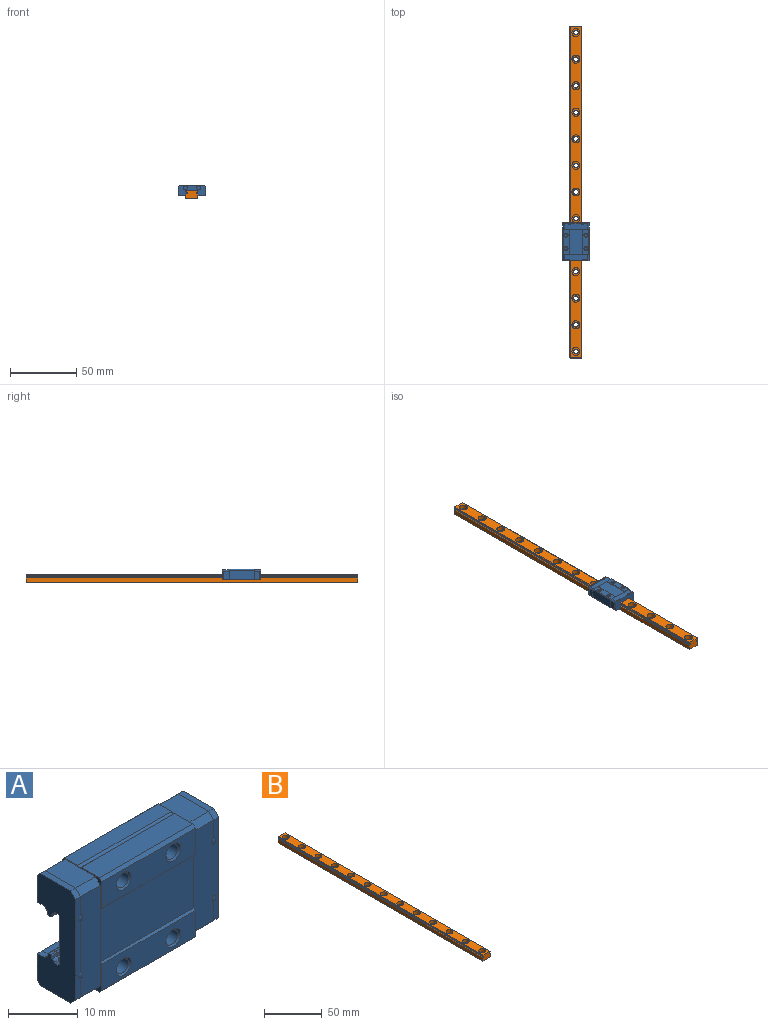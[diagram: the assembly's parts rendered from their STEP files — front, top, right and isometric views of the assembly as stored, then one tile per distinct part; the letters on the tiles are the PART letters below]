
ASSEMBLY  parts=2 mates=1
PART A: 239 faces, bbox 29x8.1x20.1 mm
  f0: plane 0.11x0.01mm, normal (0,0,1), area 0mm2, adj f1,f2,f238
  f1: revolved ~0.04x0.02mm, area 0mm2, adj f0,f2,f238
  f2: plane 17.72x5.12mm, normal (0,-1,0), area 86.8mm2, adj f0,f1,f3,f39,f40,f41,f42,f78
  f3: plane 4x1mm, normal (0,-0.71,0.71), area 5.7mm2, adj f2,f4,f87,f89
  f4: plane 6.1x4mm, normal (0,0,1), area 24.4mm2, adj f3,f5,f87,f89
  f5: plane 4x0.6mm, normal (0,0.71,0.71), area 3.4mm2, adj f4,f6,f87,f89
  f6: plane 4.7x4mm, normal (0,1,0), area 18.8mm2, adj f5,f7,f87,f89
  f7: plane 4x1.41mm, normal (0,0,-1), area 5.6mm2, adj f6,f8,f87,f89
  f8: cylinder r=0.2mm len=4mm, axis (-1,0,0), area 0.9mm2, adj f7,f9,f87,f89
  f9: cylinder r=1mm len=4mm, axis (-1,0,0), area 2.3mm2, adj f8,f10,f87,f89
  f10: cylinder r=0.2mm len=4mm, axis (-1,0,0), area 0.7mm2, adj f9,f11,f87,f89
  f11: plane 4x0.32mm, normal (0,1,-0.09), area 1.3mm2, adj f10,f12,f87,f89
  f12: cylinder r=0.2mm len=4mm, axis (1,0,0), area 1.2mm2, adj f11,f13,f87,f89
  f13: plane 4x0.41mm, normal (0,0,-1), area 1.7mm2, adj f12,f14,f87,f89
  f14: cylinder r=0.2mm len=4mm, axis (-1,0,0), area 1.2mm2, adj f13,f15,f87,f89
  f15: plane 4x0.32mm, normal (0,-1,-0.09), area 1.3mm2, adj f14,f16,f87,f89
  f16: cylinder r=0.2mm len=4mm, axis (-1,0,0), area 0.7mm2, adj f15,f17,f87,f89
  f17: cylinder r=1mm len=4mm, axis (-1,0,0), area 2.3mm2, adj f16,f18,f87,f89
  f18: cylinder r=0.2mm len=4mm, axis (-1,0,0), area 0.9mm2, adj f17,f19,f87,f89
  f19: plane 4x0.51mm, normal (0,0,-1), area 2mm2, adj f18,f20,f87,f89
  f20: plane 4x0.4mm, normal (0,0.71,-0.71), area 2.3mm2, adj f19,f21,f87,f89
  f21: plane 8.2x4mm, normal (0,1,0), area 32.8mm2, adj f20,f22,f87,f89
  f22: plane 4x0.4mm, normal (0,0.71,0.71), area 2.3mm2, adj f21,f23,f87,f89
  f23: plane 4x0.51mm, normal (0,0,1), area 2mm2, adj f22,f24,f87,f89
  f24: cylinder r=0.2mm len=4mm, axis (-1,0,0), area 0.9mm2, adj f23,f25,f87,f89
  f25: cylinder r=1mm len=4mm, axis (-1,0,0), area 2.3mm2, adj f24,f26,f87,f89
  f26: cylinder r=0.2mm len=4mm, axis (-1,0,0), area 0.7mm2, adj f25,f27,f87,f89
  f27: plane 4x0.32mm, normal (0,-1,0.09), area 1.3mm2, adj f26,f28,f87,f89
  f28: cylinder r=0.2mm len=4mm, axis (-1,0,0), area 1.2mm2, adj f27,f29,f87,f89
  f29: plane 4x0.41mm, normal (0,0,1), area 1.7mm2, adj f28,f30,f87,f89
  f30: cylinder r=0.2mm len=4mm, axis (-1,0,0), area 1.2mm2, adj f29,f31,f87,f89
  f31: plane 4x0.32mm, normal (0,1,0.09), area 1.3mm2, adj f30,f32,f87,f89
  f32: cylinder r=0.2mm len=4mm, axis (-1,0,0), area 0.7mm2, adj f31,f33,f87,f89
  f33: cylinder r=1mm len=4mm, axis (-1,0,0), area 2.3mm2, adj f32,f34,f87,f89
  f34: cylinder r=0.2mm len=4mm, axis (-1,0,0), area 0.9mm2, adj f33,f35,f87,f89
  f35: plane 4x1.41mm, normal (0,0,1), area 5.6mm2, adj f34,f36,f87,f89
  f36: plane 4.7x4mm, normal (0,1,0), area 18.8mm2, adj f35,f37,f87,f89
  f37: plane 4x0.6mm, normal (0,0.71,-0.71), area 3.4mm2, adj f36,f38,f87,f89
  f38: plane 6.1x4mm, normal (0,0,-1), area 24.4mm2, adj f37,f87,f88,f89
  f39: plane 0.96x0.1mm, normal (-1,0,0), area 0.1mm2, adj f2,f40,f238
  f40: plane 0.54x0.05mm, normal (0,0,-1), area 0mm2, adj f2,f39,f238
  f41: revolved ~0.7x0.04mm, area 0mm2, adj f2,f238
  f42: plane 1x1mm, normal (0,-0.71,0.71), area 1.4mm2, adj f2,f43,f78,f80
  f43: plane 6.1x1mm, normal (0,0,1), area 6.1mm2, adj f42,f44,f78,f80
  f44: plane 1x0.6mm, normal (0,0.71,0.71), area 0.8mm2, adj f43,f45,f78,f80
  f45: plane 4.7x1mm, normal (0,1,0), area 4.7mm2, adj f44,f46,f78,f80
  f46: plane 1.41x1mm, normal (0,0,-1), area 1.4mm2, adj f45,f47,f78,f80
  f47: cylinder r=0.2mm len=1mm, axis (-1,0,0), area 0.2mm2, adj f46,f48,f78,f80
  f48: cylinder r=1mm len=1mm, axis (-1,0,0), area 0.6mm2, adj f47,f49,f78,f80
  f49: cylinder r=0.2mm len=1mm, axis (-1,0,0), area 0.2mm2, adj f48,f50,f78,f80
  f50: plane 1x0.32mm, normal (0,1,-0.09), area 0.3mm2, adj f49,f51,f78,f80
  f51: cylinder r=0.2mm len=1mm, axis (-1,0,0), area 0.3mm2, adj f50,f52,f78,f80
  f52: plane 1x0.41mm, normal (0,0,-1), area 0.4mm2, adj f51,f53,f78,f80
  f53: cylinder r=0.2mm len=1mm, axis (-1,0,0), area 0.3mm2, adj f52,f54,f78,f80
  f54: plane 1x0.32mm, normal (0,-1,-0.09), area 0.3mm2, adj f53,f55,f78,f80
  f55: cylinder r=0.2mm len=1mm, axis (-1,0,0), area 0.2mm2, adj f54,f56,f78,f80
  f56: cylinder r=1mm len=1mm, axis (-1,0,0), area 0.6mm2, adj f55,f57,f78,f80
  f57: cylinder r=0.2mm len=1mm, axis (-1,0,0), area 0.2mm2, adj f56,f58,f78,f80
  f58: plane 1x0.51mm, normal (0,0,-1), area 0.5mm2, adj f57,f59,f78,f80
  f59: plane 1x0.4mm, normal (0,0.71,-0.71), area 0.6mm2, adj f58,f60,f78,f80
  f60: plane 8.2x1mm, normal (0,1,0), area 8.2mm2, adj f59,f61,f78,f80
  f61: plane 1x0.4mm, normal (0,0.71,0.71), area 0.6mm2, adj f60,f62,f78,f80
  f62: plane 1x0.51mm, normal (0,0,1), area 0.5mm2, adj f61,f63,f78,f80
  f63: cylinder r=0.2mm len=1mm, axis (-1,0,0), area 0.2mm2, adj f62,f64,f78,f80
  f64: cylinder r=1mm len=1mm, axis (-1,0,0), area 0.6mm2, adj f63,f65,f78,f80
  f65: cylinder r=0.2mm len=1mm, axis (-1,0,0), area 0.2mm2, adj f64,f66,f78,f80
  f66: plane 1x0.32mm, normal (0,-1,0.09), area 0.3mm2, adj f65,f67,f78,f80
  f67: cylinder r=0.2mm len=1mm, axis (-1,0,0), area 0.3mm2, adj f66,f68,f78,f80
  f68: plane 1x0.41mm, normal (0,0,1), area 0.4mm2, adj f67,f69,f78,f80
  f69: cylinder r=0.2mm len=1mm, axis (-1,0,0), area 0.3mm2, adj f68,f70,f78,f80
  f70: plane 1x0.32mm, normal (0,1,0.09), area 0.3mm2, adj f69,f71,f78,f80
  f71: cylinder r=0.2mm len=1mm, axis (-1,0,0), area 0.2mm2, adj f70,f72,f78,f80
  f72: cylinder r=1mm len=1mm, axis (-1,0,0), area 0.6mm2, adj f71,f73,f78,f80
  f73: cylinder r=0.2mm len=1mm, axis (-1,0,0), area 0.2mm2, adj f72,f74,f78,f80
  f74: plane 1.41x1mm, normal (0,0,1), area 1.4mm2, adj f73,f75,f78,f80
  f75: plane 4.7x1mm, normal (0,1,0), area 4.7mm2, adj f74,f76,f78,f80
  f76: plane 1x0.6mm, normal (0,0.71,-0.71), area 0.8mm2, adj f75,f77,f78,f80
  f77: plane 6.1x1mm, normal (0,0,-1), area 6.1mm2, adj f76,f78,f79,f80
  f78: plane 19.6x7.7mm, normal (1,0,0), area 112.1mm2, adj f2,f42,f43,f44,f45,f46,f47,f48
  f79: plane 1x1mm, normal (0,-0.71,-0.71), area 1.4mm2, adj f2,f77,f78,f80
  f80: plane 19.6x7.7mm, normal (-1,0,0), area 96.6mm2, adj f2,f42,f43,f44,f45,f46,f47,f48
  f81: revolved ~0.7x0.04mm, area 0mm2, adj f2,f86
  f82: revolved ~0.04x0.02mm, area 0mm2, adj f2,f83,f86
  f83: plane 0.11x0.01mm, normal (0,0,-1), area 0mm2, adj f2,f82,f86
  f84: plane 0.54x0.05mm, normal (0,0,1), area 0mm2, adj f2,f85,f86
  f85: plane 0.96x0.1mm, normal (-1,0,0), area 0.1mm2, adj f2,f84,f86
  f86: cone r=1.57mm half-angle=5deg, axis (-1,0,0), area 0.6mm2, adj f2,f80,f81,f82,f83,f84,f85,f87
  f87: plane 19.6x7.7mm, normal (1,0,0), area 96.6mm2, adj f2,f3,f4,f5,f6,f7,f8,f9
  f88: plane 4x1mm, normal (0,-0.71,-0.71), area 5.7mm2, adj f2,f38,f87,f89
  f89: plane 19.6x7.7mm, normal (-1,0,0), area 108mm2, adj f2,f3,f4,f5,f6,f7,f8,f9
  f90: cylinder r=0.8mm len=1.6mm, axis (-1,0,0), area 0mm2, adj f89,f91
  f91: plane 20x8mm, normal (1,0,0), area 115mm2, adj f90,f92,f182,f183,f184,f185,f186,f187
  f92: cylinder r=0.2mm len=18.9mm, axis (-1,0,0), area 3.5mm2, adj f91,f93,f182,f236
  f93: plane 20x8mm, normal (-1,0,0), area 115mm2, adj f92,f94,f181,f182,f183,f184,f185,f186
  f94: cylinder r=0.8mm len=1.6mm, axis (1,0,0), area 0mm2, adj f93,f95
  f95: plane 19.6x7.7mm, normal (1,0,0), area 108mm2, adj f94,f96,f144,f145,f146,f147,f148,f149
  f96: cylinder r=0.2mm len=4mm, axis (1,0,0), area 0.7mm2, adj f95,f97,f144,f180
  f97: plane 19.6x7.7mm, normal (-1,0,0), area 96.6mm2, adj f96,f98,f142,f144,f145,f146,f147,f148
  f98: cone r=1.6mm half-angle=5deg, axis (1,0,0), area 0.6mm2, adj f97,f99,f100,f140,f141,f167
  f99: revolved ~0.7x0.04mm, area 0mm2, adj f98,f100
  f100: plane 17.72x1.12mm, normal (0,-1,0), area 17mm2, adj f98,f99,f101,f102,f138,f139,f140,f142
  f101: revolved ~0.7x0.04mm, area 0mm2, adj f100,f142
  f102: plane 1x1mm, normal (0,-0.71,-0.71), area 1.4mm2, adj f100,f103,f138,f140
  f103: plane 6.1x1mm, normal (0,0,-1), area 6.1mm2, adj f102,f104,f138,f140
  f104: plane 1x0.6mm, normal (0,0.71,-0.71), area 0.8mm2, adj f103,f105,f138,f140
  f105: plane 4.7x1mm, normal (0,1,0), area 4.7mm2, adj f104,f106,f138,f140
  f106: plane 1.41x1mm, normal (0,0,1), area 1.4mm2, adj f105,f107,f138,f140
  f107: cylinder r=0.2mm len=1mm, axis (1,0,0), area 0.2mm2, adj f106,f108,f138,f140
  f108: cylinder r=1mm len=1mm, axis (1,0,0), area 0.6mm2, adj f107,f109,f138,f140
  f109: cylinder r=0.2mm len=1mm, axis (1,0,0), area 0.2mm2, adj f108,f110,f138,f140
  f110: plane 1x0.32mm, normal (0,1,0.09), area 0.3mm2, adj f109,f111,f138,f140
  f111: cylinder r=0.2mm len=1mm, axis (1,0,0), area 0.3mm2, adj f110,f112,f138,f140
  f112: plane 1x0.41mm, normal (0,0,1), area 0.4mm2, adj f111,f113,f138,f140
  f113: cylinder r=0.2mm len=1mm, axis (1,0,0), area 0.3mm2, adj f112,f114,f138,f140
  f114: plane 1x0.32mm, normal (0,-1,0.09), area 0.3mm2, adj f113,f115,f138,f140
  f115: cylinder r=0.2mm len=1mm, axis (1,0,0), area 0.2mm2, adj f114,f116,f138,f140
  f116: cylinder r=1mm len=1mm, axis (1,0,0), area 0.6mm2, adj f115,f117,f138,f140
  f117: cylinder r=0.2mm len=1mm, axis (1,0,0), area 0.2mm2, adj f116,f118,f138,f140
  f118: plane 1x0.51mm, normal (0,0,1), area 0.5mm2, adj f117,f119,f138,f140
  f119: plane 1x0.4mm, normal (0,0.71,0.71), area 0.6mm2, adj f118,f120,f138,f140
  f120: plane 8.2x1mm, normal (0,1,0), area 8.2mm2, adj f119,f121,f138,f140
  f121: plane 1x0.4mm, normal (0,0.71,-0.71), area 0.6mm2, adj f120,f122,f138,f140
  f122: plane 1x0.51mm, normal (0,0,-1), area 0.5mm2, adj f121,f123,f138,f140
  f123: cylinder r=0.2mm len=1mm, axis (1,0,0), area 0.2mm2, adj f122,f124,f138,f140
  f124: cylinder r=1mm len=1mm, axis (1,0,0), area 0.6mm2, adj f123,f125,f138,f140
  f125: cylinder r=0.2mm len=1mm, axis (1,0,0), area 0.2mm2, adj f124,f126,f138,f140
  f126: plane 1x0.32mm, normal (0,-1,-0.09), area 0.3mm2, adj f125,f127,f138,f140
  f127: cylinder r=0.2mm len=1mm, axis (1,0,0), area 0.3mm2, adj f126,f128,f138,f140
  f128: plane 1x0.41mm, normal (0,0,-1), area 0.4mm2, adj f127,f129,f138,f140
  f129: cylinder r=0.2mm len=1mm, axis (1,0,0), area 0.3mm2, adj f128,f130,f138,f140
  f130: plane 1x0.32mm, normal (0,1,-0.09), area 0.3mm2, adj f129,f131,f138,f140
  f131: cylinder r=0.2mm len=1mm, axis (1,0,0), area 0.2mm2, adj f130,f132,f138,f140
  f132: cylinder r=1mm len=1mm, axis (1,0,0), area 0.6mm2, adj f131,f133,f138,f140
  f133: cylinder r=0.2mm len=1mm, axis (1,0,0), area 0.2mm2, adj f132,f134,f138,f140
  f134: plane 1.41x1mm, normal (0,0,-1), area 1.4mm2, adj f133,f135,f138,f140
  f135: plane 4.7x1mm, normal (0,1,0), area 4.7mm2, adj f134,f136,f138,f140
  f136: plane 1x0.6mm, normal (0,0.71,0.71), area 0.8mm2, adj f135,f137,f138,f140
  f137: plane 6.1x1mm, normal (0,0,1), area 6.1mm2, adj f136,f138,f139,f140
  f138: plane 19.6x7.7mm, normal (-1,0,0), area 112.1mm2, adj f100,f102,f103,f104,f105,f106,f107,f108
  f139: plane 1x1mm, normal (0,-0.71,0.71), area 1.4mm2, adj f100,f137,f138,f140
  f140: plane 19.6x7.7mm, normal (1,0,0), area 96.6mm2, adj f98,f100,f102,f103,f104,f105,f106,f107
  f141: plane 1.11x0.1mm, normal (1,0,0), area 0.1mm2, adj f98,f167
  f142: cone r=1.6mm half-angle=5deg, axis (1,0,0), area 0.6mm2, adj f97,f100,f101,f140,f143,f167
  f143: plane 1.11x0.1mm, normal (1,0,0), area 0.1mm2, adj f142,f167
  f144: cylinder r=1mm len=4mm, axis (1,0,0), area 2.3mm2, adj f95,f96,f97,f145
  f145: cylinder r=0.2mm len=4mm, axis (1,0,0), area 0.9mm2, adj f95,f97,f144,f146
  f146: plane 4x0.51mm, normal (0,0,-1), area 2mm2, adj f95,f97,f145,f147
  f147: plane 4x0.4mm, normal (0,0.71,-0.71), area 2.3mm2, adj f95,f97,f146,f148
  f148: plane 8.2x4mm, normal (0,1,0), area 32.8mm2, adj f95,f97,f147,f149
  f149: plane 4x0.4mm, normal (0,0.71,0.71), area 2.3mm2, adj f95,f97,f148,f150
  f150: plane 4x0.51mm, normal (0,0,1), area 2mm2, adj f95,f97,f149,f151
  f151: cylinder r=0.2mm len=4mm, axis (1,0,0), area 0.9mm2, adj f95,f97,f150,f152
  f152: cylinder r=1mm len=4mm, axis (1,0,0), area 2.3mm2, adj f95,f97,f151,f153
  f153: cylinder r=0.2mm len=4mm, axis (1,0,0), area 0.7mm2, adj f95,f97,f152,f154
  f154: plane 4x0.32mm, normal (0,-1,0.09), area 1.3mm2, adj f95,f97,f153,f155
  f155: cylinder r=0.2mm len=4mm, axis (1,0,0), area 1.2mm2, adj f95,f97,f154,f156
  f156: plane 4x0.41mm, normal (0,0,1), area 1.7mm2, adj f95,f97,f155,f157
  f157: cylinder r=0.2mm len=4mm, axis (1,0,0), area 1.2mm2, adj f95,f97,f156,f158
  f158: plane 4x0.32mm, normal (0,1,0.09), area 1.3mm2, adj f95,f97,f157,f159
  f159: cylinder r=0.2mm len=4mm, axis (1,0,0), area 0.7mm2, adj f95,f97,f158,f160
  f160: cylinder r=1mm len=4mm, axis (1,0,0), area 2.3mm2, adj f95,f97,f159,f161
  f161: cylinder r=0.2mm len=4mm, axis (1,0,0), area 0.9mm2, adj f95,f97,f160,f162
  f162: plane 4x1.41mm, normal (0,0,1), area 5.6mm2, adj f95,f97,f161,f163
  f163: plane 4.7x4mm, normal (0,1,0), area 18.8mm2, adj f95,f97,f162,f164
  f164: plane 4x0.6mm, normal (0,0.71,-0.71), area 3.4mm2, adj f95,f97,f163,f165
  f165: plane 6.1x4mm, normal (0,0,-1), area 24.4mm2, adj f95,f97,f164,f166
  f166: plane 4x1mm, normal (0,-0.71,-0.71), area 5.7mm2, adj f95,f97,f165,f167
  f167: plane 17.6x4mm, normal (0,-1,0), area 69.8mm2, adj f95,f97,f98,f141,f142,f143,f166,f168
  f168: plane 4x1mm, normal (0,-0.71,0.71), area 5.7mm2, adj f95,f97,f167,f169
  f169: plane 6.1x4mm, normal (0,0,1), area 24.4mm2, adj f95,f97,f168,f170
  f170: plane 4x0.6mm, normal (0,0.71,0.71), area 3.4mm2, adj f95,f97,f169,f171
  f171: plane 4.7x4mm, normal (0,1,0), area 18.8mm2, adj f95,f97,f170,f172
  f172: plane 4x1.41mm, normal (0,0,-1), area 5.6mm2, adj f95,f97,f171,f173
  f173: cylinder r=0.2mm len=4mm, axis (1,0,0), area 0.9mm2, adj f95,f97,f172,f174
  f174: cylinder r=1mm len=4mm, axis (1,0,0), area 2.3mm2, adj f95,f97,f173,f175
  f175: cylinder r=0.2mm len=4mm, axis (1,0,0), area 0.7mm2, adj f95,f97,f174,f176
  f176: plane 4x0.32mm, normal (0,1,-0.09), area 1.3mm2, adj f95,f97,f175,f177
  f177: cylinder r=0.2mm len=4mm, axis (1,0,0), area 1.2mm2, adj f95,f97,f176,f178
  f178: plane 4x0.41mm, normal (0,0,-1), area 1.7mm2, adj f95,f97,f177,f179
  f179: cylinder r=0.2mm len=4mm, axis (1,0,0), area 1.2mm2, adj f95,f97,f178,f180
  f180: plane 4x0.32mm, normal (0,-1,-0.09), area 1.3mm2, adj f95,f96,f97,f179
  f181: cylinder r=0.8mm len=1.6mm, axis (1,0,0), area 0mm2, adj f93,f95
  f182: cylinder r=1mm len=18.9mm, axis (-1,0,0), area 11.1mm2, adj f91,f92,f93,f183
  f183: cylinder r=0.2mm len=18.9mm, axis (-1,0,0), area 4.3mm2, adj f91,f93,f182,f184
  f184: plane 18.9x0.51mm, normal (0,0,-1), area 9.6mm2, adj f91,f93,f183,f185
  f185: plane 18.9x0.4mm, normal (0,0.71,-0.71), area 10.7mm2, adj f91,f93,f184,f186
  f186: plane 18.9x8.2mm, normal (0,1,0), area 155mm2, adj f91,f93,f185,f187
  f187: plane 18.9x0.4mm, normal (0,0.71,0.71), area 10.7mm2, adj f91,f93,f186,f188
  f188: plane 18.9x0.51mm, normal (0,0,1), area 9.6mm2, adj f91,f93,f187,f189
  f189: cylinder r=0.2mm len=18.9mm, axis (-1,0,0), area 4.3mm2, adj f91,f93,f188,f190
  f190: cylinder r=1mm len=18.9mm, axis (-1,0,0), area 11.1mm2, adj f91,f93,f189,f191
  f191: cylinder r=0.2mm len=18.9mm, axis (-1,0,0), area 3.5mm2, adj f91,f93,f190,f192
  f192: plane 18.9x0.32mm, normal (0,-1,0.09), area 6mm2, adj f91,f93,f191,f193
  f193: cylinder r=0.2mm len=18.9mm, axis (-1,0,0), area 5.6mm2, adj f91,f93,f192,f194
  f194: plane 18.9x0.41mm, normal (0,0,1), area 7.8mm2, adj f91,f93,f193,f195
  f195: cylinder r=0.2mm len=18.9mm, axis (-1,0,0), area 5.6mm2, adj f91,f93,f194,f196
  f196: plane 18.9x0.32mm, normal (0,1,0.09), area 6mm2, adj f91,f93,f195,f197
  f197: cylinder r=0.2mm len=18.9mm, axis (-1,0,0), area 3.5mm2, adj f91,f93,f196,f198
  f198: cylinder r=1mm len=18.9mm, axis (-1,0,0), area 11.1mm2, adj f91,f93,f197,f199
  f199: cylinder r=0.2mm len=18.9mm, axis (-1,0,0), area 4.3mm2, adj f91,f93,f198,f200
  f200: plane 18.9x1.41mm, normal (0,0,1), area 26.6mm2, adj f91,f93,f199,f201
  f201: plane 18.9x5mm, normal (0,1,0), area 94.5mm2, adj f91,f93,f200,f202
  f202: plane 18.9x0.5mm, normal (0,0.71,-0.71), area 13.4mm2, adj f91,f93,f201,f203
  f203: plane 18.9x7mm, normal (0,0,-1), area 132.3mm2, adj f91,f93,f202,f204
  f204: plane 18.9x0.5mm, normal (0,-0.71,-0.71), area 13.4mm2, adj f91,f93,f203,f205
  f205: plane 18.9x4.6mm, normal (0,-1,0), area 72.8mm2, adj f91,f93,f204,f206,f209,f212
  f206: cone r=1.23mm half-angle=45deg, axis (0,-1,0), area 3.3mm2, adj f205,f207
  f207: cylinder r=1.23mm len=3.48mm, axis (0,-1,0), area 26.9mm2, adj f206,f208
  f208: cone r=1.23mm half-angle=63.4deg, axis (0,-1,0), area 5.3mm2, adj f207
  f209: cone r=1.23mm half-angle=45deg, axis (0,-1,0), area 3.3mm2, adj f205,f210
  f210: cylinder r=1.23mm len=3.48mm, axis (0,-1,0), area 26.9mm2, adj f209,f211
  f211: cone r=1.23mm half-angle=63.4deg, axis (0,-1,0), area 5.3mm2, adj f210
  f212: plane 18.9x0.3mm, normal (0,-0.71,0.71), area 8mm2, adj f91,f93,f205,f213
  f213: plane 18.9x9.2mm, normal (0,-1,0), area 173.9mm2, adj f91,f93,f212,f214
  f214: plane 18.9x0.3mm, normal (0,-0.71,-0.71), area 8mm2, adj f91,f93,f213,f215
  f215: plane 18.9x4.6mm, normal (0,-1,0), area 72.8mm2, adj f91,f93,f214,f216,f219,f222
  f216: cone r=1.23mm half-angle=45deg, axis (0,-1,0), area 3.3mm2, adj f215,f217
  f217: cylinder r=1.23mm len=3.48mm, axis (0,-1,0), area 26.9mm2, adj f216,f218
  f218: cone r=1.23mm half-angle=63.4deg, axis (0,-1,0), area 5.3mm2, adj f217
  f219: cone r=1.23mm half-angle=45deg, axis (0,-1,0), area 3.3mm2, adj f215,f220
  f220: cylinder r=1.23mm len=3.48mm, axis (0,-1,0), area 26.9mm2, adj f219,f221
  f221: cone r=1.23mm half-angle=63.4deg, axis (0,-1,0), area 5.3mm2, adj f220
  f222: plane 18.9x0.5mm, normal (0,-0.71,0.71), area 13.4mm2, adj f91,f93,f215,f223
  f223: plane 18.9x3.65mm, normal (0,0,1), area 69.1mm2, adj f91,f93,f222,f224
  f224: cylinder r=0.4mm len=18.9mm, axis (1,0,0), area 15.8mm2, adj f91,f93,f223,f225
  f225: plane 18.9x2.65mm, normal (0,0,1), area 50.2mm2, adj f91,f93,f224,f226
  f226: plane 18.9x0.5mm, normal (0,0.71,0.71), area 13.4mm2, adj f91,f93,f225,f227
  f227: plane 18.9x5mm, normal (0,1,0), area 94.5mm2, adj f91,f93,f226,f228
  f228: plane 18.9x1.41mm, normal (0,0,-1), area 26.6mm2, adj f91,f93,f227,f229
  f229: cylinder r=0.2mm len=18.9mm, axis (-1,0,0), area 4.3mm2, adj f91,f93,f228,f230
  f230: cylinder r=1mm len=18.9mm, axis (-1,0,0), area 11.1mm2, adj f91,f93,f229,f231
  f231: cylinder r=0.2mm len=18.9mm, axis (-1,0,0), area 3.5mm2, adj f91,f93,f230,f232
  f232: plane 18.9x0.32mm, normal (0,1,-0.09), area 6mm2, adj f91,f93,f231,f233
  f233: cylinder r=0.2mm len=18.9mm, axis (-1,0,0), area 5.6mm2, adj f91,f93,f232,f234
  f234: plane 18.9x0.41mm, normal (0,0,-1), area 7.8mm2, adj f91,f93,f233,f235
  f235: cylinder r=0.2mm len=18.9mm, axis (-1,0,0), area 5.6mm2, adj f91,f93,f234,f236
  f236: plane 18.9x0.32mm, normal (0,-1,-0.09), area 6mm2, adj f91,f92,f93,f235
  f237: cylinder r=0.8mm len=1.6mm, axis (-1,0,0), area 0mm2, adj f89,f91
  f238: cone r=1.57mm half-angle=5deg, axis (-1,0,0), area 0.6mm2, adj f0,f1,f2,f39,f40,f41,f80,f87
PART B: 61 faces, bbox 9x250x6.5 mm
  f0: plane 250x0.8mm, normal (-1,0,0), area 200mm2, adj f1,f19,f20,f21
  f1: plane 250x0.53mm, normal (0,0,1), area 133.4mm2, adj f0,f2,f20,f21
  f2: cylinder r=1mm len=250mm, axis (0,1,0), area 226.6mm2, adj f1,f3,f20,f21
  f3: plane 250x3.18mm, normal (-1,0,0), area 794.6mm2, adj f2,f4,f20,f21
  f4: plane 250x0.35mm, normal (-0.71,0,-0.71), area 125mm2, adj f3,f5,f20,f21
  f5: plane 250x8.29mm, normal (0,0,-1), area 1948.1mm2, adj f4,f6,f20,f21,f22,f25,f28,f31
  f6: plane 250x0.35mm, normal (0.71,0,-0.71), area 125mm2, adj f5,f7,f20,f21
  f7: plane 250x3.18mm, normal (1,0,0), area 794.6mm2, adj f6,f8,f20,f21
  f8: cylinder r=1mm len=250mm, axis (0,1,0), area 226.6mm2, adj f7,f9,f20,f21
  f9: plane 250x0.53mm, normal (0,0,1), area 133.4mm2, adj f8,f10,f20,f21
  f10: plane 250x0.8mm, normal (1,0,0), area 200mm2, adj f9,f11,f20,f21
  f11: plane 250x0.53mm, normal (0,0,-1), area 133.4mm2, adj f10,f12,f20,f21
  f12: cylinder r=1mm len=250mm, axis (0,1,0), area 226.6mm2, adj f11,f13,f20,f21
  f13: plane 250x0.68mm, normal (1,0,0), area 169.6mm2, adj f12,f14,f20,f21
  f14: plane 250x0.35mm, normal (0.71,0,0.71), area 125mm2, adj f13,f15,f20,f21
  f15: plane 250x8.29mm, normal (0,0,1), area 1705.7mm2, adj f14,f16,f20,f21,f24,f27,f30,f33
  f16: plane 250x0.35mm, normal (-0.71,0,0.71), area 125mm2, adj f15,f17,f20,f21
  f17: plane 250x0.68mm, normal (-1,0,0), area 169.6mm2, adj f16,f18,f20,f21
  f18: cylinder r=1mm len=250mm, axis (0,1,0), area 226.6mm2, adj f17,f19,f20,f21
  f19: plane 250x0.53mm, normal (0,0,-1), area 133.4mm2, adj f0,f18,f20,f21
  f20: plane 9x6.5mm, normal (0,-1,0), area 55.3mm2, adj f0,f1,f2,f3,f4,f5,f6,f7
  f21: plane 9x6.5mm, normal (0,1,0), area 55.3mm2, adj f0,f1,f2,f3,f4,f5,f6,f7
  f22: cylinder r=1.75mm len=3.5mm, axis (0,0,1), area 33mm2, adj f5,f23
  f23: plane 6x6mm, normal (0,0,1), area 18.7mm2, adj f22,f24
  f24: cylinder r=3mm len=6mm, axis (0,0,1), area 66mm2, adj f15,f23
  f25: cylinder r=1.75mm len=3.5mm, axis (0,0,1), area 33mm2, adj f5,f26
  f26: plane 6x6mm, normal (0,0,1), area 18.7mm2, adj f25,f27
  f27: cylinder r=3mm len=6mm, axis (0,0,1), area 66mm2, adj f15,f26
  f28: cylinder r=1.75mm len=3.5mm, axis (0,0,1), area 33mm2, adj f5,f29
  f29: plane 6x6mm, normal (0,0,1), area 18.7mm2, adj f28,f30
  f30: cylinder r=3mm len=6mm, axis (0,0,1), area 66mm2, adj f15,f29
  f31: cylinder r=1.75mm len=3.5mm, axis (0,0,1), area 33mm2, adj f5,f32
  f32: plane 6x6mm, normal (0,0,1), area 18.7mm2, adj f31,f33
  f33: cylinder r=3mm len=6mm, axis (0,0,1), area 66mm2, adj f15,f32
  f34: cylinder r=1.75mm len=3.5mm, axis (0,0,1), area 33mm2, adj f5,f35
  f35: plane 6x6mm, normal (0,0,1), area 18.7mm2, adj f34,f36
  f36: cylinder r=3mm len=6mm, axis (0,0,1), area 66mm2, adj f15,f35
  f37: cylinder r=1.75mm len=3.5mm, axis (0,0,1), area 33mm2, adj f5,f38
  f38: plane 6x6mm, normal (0,0,1), area 18.7mm2, adj f37,f39
  f39: cylinder r=3mm len=6mm, axis (0,0,1), area 66mm2, adj f15,f38
  f40: cylinder r=1.75mm len=3.5mm, axis (0,0,1), area 33mm2, adj f5,f41
  f41: plane 6x6mm, normal (0,0,1), area 18.7mm2, adj f40,f42
  f42: cylinder r=3mm len=6mm, axis (0,0,1), area 66mm2, adj f15,f41
  f43: cylinder r=1.75mm len=3.5mm, axis (0,0,1), area 33mm2, adj f5,f44
  f44: plane 6x6mm, normal (0,0,1), area 18.7mm2, adj f43,f45
  f45: cylinder r=3mm len=6mm, axis (0,0,1), area 66mm2, adj f15,f44
  f46: cylinder r=1.75mm len=3.5mm, axis (0,0,1), area 33mm2, adj f5,f47
  f47: plane 6x6mm, normal (0,0,1), area 18.7mm2, adj f46,f48
  f48: cylinder r=3mm len=6mm, axis (0,0,1), area 66mm2, adj f15,f47
  f49: cylinder r=1.75mm len=3.5mm, axis (0,0,1), area 33mm2, adj f5,f50
  f50: plane 6x6mm, normal (0,0,1), area 18.7mm2, adj f49,f51
  f51: cylinder r=3mm len=6mm, axis (0,0,1), area 66mm2, adj f15,f50
  f52: cylinder r=1.75mm len=3.5mm, axis (0,0,1), area 33mm2, adj f5,f53
  f53: plane 6x6mm, normal (0,0,1), area 18.7mm2, adj f52,f54
  f54: cylinder r=3mm len=6mm, axis (0,0,1), area 66mm2, adj f15,f53
  f55: cylinder r=1.75mm len=3.5mm, axis (0,0,1), area 33mm2, adj f5,f56
  f56: plane 6x6mm, normal (0,0,1), area 18.7mm2, adj f55,f57
  f57: cylinder r=3mm len=6mm, axis (0,0,1), area 66mm2, adj f15,f56
  f58: cylinder r=1.75mm len=3.5mm, axis (0,0,1), area 33mm2, adj f5,f59
  f59: plane 6x6mm, normal (0,0,1), area 18.7mm2, adj f58,f60
  f60: cylinder r=3mm len=6mm, axis (0,0,1), area 66mm2, adj f15,f59
PLACE A rot(axis=(-0.58,0.58,-0.58),120deg) t=(0.05,-22.99,2)mm
PLACE B rot(axis=(0,-1,0),0deg) t=(0,125,3.25)mm
MATE slider A.f25 <-> B.f2  axis (0,1,0) through (-4.75,-27.99,4.5)mm
